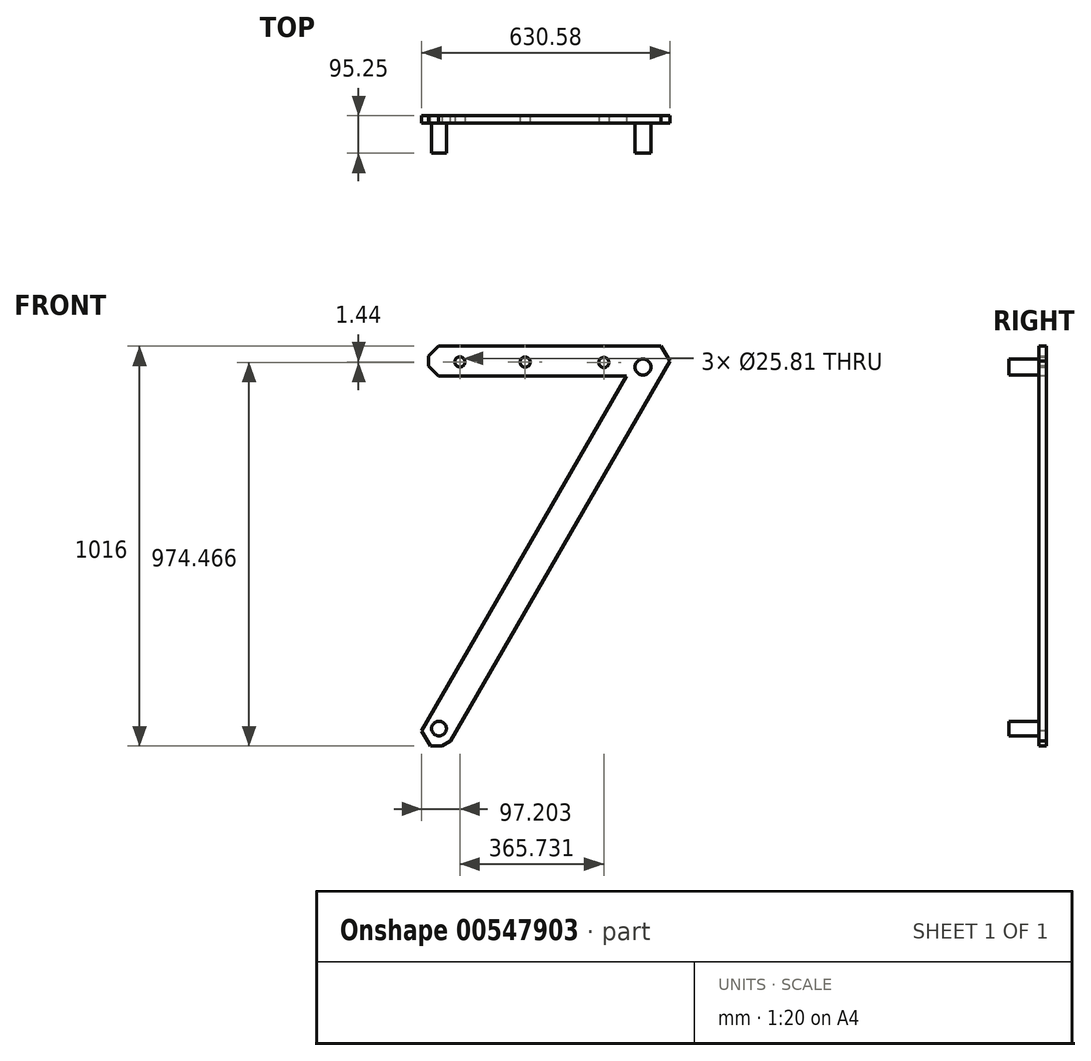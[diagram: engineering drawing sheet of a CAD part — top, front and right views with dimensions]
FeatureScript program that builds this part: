
annotation { "Feature Type Name" : "Feature", "Feature Type Description" : "" }
export const myFeature = defineFeature(function(context is Context, id is Id, definition is map)
    precondition{}
    {
        {
            var Q0;
            Q0=qCreatedBy(makeId("Front.planeOp"),FACE);
            var sketch = newSketch(context, id + "F0", { "sketchPlane" : qUnion([Q0])});
            skLineSegment(sketch, "E0", {"start": v(227.3, 546.1) * mm, "end": v(315.3, 546.1) * mm});
            skLineSegment(sketch, "E1", {"start": v(315.3, 546.1) * mm, "end": v(-271.3, -469.9) * mm});
            skLineSegment(sketch, "E2", {"start": v(-271.3, -469.9) * mm, "end": v(-359.29, -469.9) * mm});
            skLineSegment(sketch, "E3", {"start": v(-359.29, -469.9) * mm, "end": v(227.3, 546.1) * mm});
            skLineSegment(sketch, "E4", {"start": v(-66, 38.1) * mm, "end": v(0, 0) * mm, "construction": true});
            skSolve(sketch);
        }
        {
            var Q0;
            Q0 = qSketchRegion(id + "F0", true);
            extrude(context, id + "F1", {"entities" : qUnion([Q0]), "depth" : 19.05 * mm, "offsetDistance" : 25.4 * mm});
        }
        {
            var Q0;
            Q0=makeQuery(id+"F1.opExtrude","CAP_FACE",FACE,{"disambiguationData":[OSD([sQuery(id+"F0.wireOp",EDGE,"E0"),sQuery(id+"F0.wireOp",EDGE,"E1"),sQuery(id+"F0.wireOp",EDGE,"E2"),sQuery(id+"F0.wireOp",EDGE,"E3")])],"isStart":false});
            var sketch = newSketch(context, id + "F2", { "sketchPlane" : qUnion([Q0])});
            skLineSegment(sketch, "E5", {"start": v(-319.7, 546.1) * mm, "end": v(227.3, 546.1) * mm});
            skLineSegment(sketch, "E6", {"start": v(227.3, 546.1) * mm, "end": v(183.3, 469.9) * mm});
            skLineSegment(sketch, "E7", {"start": v(183.3, 469.9) * mm, "end": v(-319.7, 469.9) * mm});
            skLineSegment(sketch, "E8", {"start": v(-319.7, 469.9) * mm, "end": v(-319.7, 546.1) * mm});
            skSolve(sketch);
        }
        {
            var Q0;
            Q0 = qSketchRegion(id + "F2", true);
            var Q1;
            Q1=makeQuery(id+"F1.opExtrude","CAP_FACE",FACE,{"disambiguationData":[OSD([sQuery(id+"F0.wireOp",EDGE,"E0"),sQuery(id+"F0.wireOp",EDGE,"E1"),sQuery(id+"F0.wireOp",EDGE,"E2"),sQuery(id+"F0.wireOp",EDGE,"E3")])],"isStart":true});
            extrude(context, id + "F3", {"entities" : qUnion([Q0]), "operationType" : NewBodyOperationType.ADD, "endBound" : BoundingType.UP_TO_SURFACE, "oppositeDirection" : true, "depth" : 19.05 * mm, "endBoundEntityFace" : qUnion([Q1]), "offsetDistance" : 25.4 * mm});
        }
        {
            var Q0;
            Q0=makeQuery(id+"F3.boolean.opBoolean","MERGE",FACE,{"derivedFrom":[makeQuery(id+"F1.opExtrude","CAP_FACE",FACE,{"disambiguationData":[OSD([sQuery(id+"F0.wireOp",EDGE,"E0"),sQuery(id+"F0.wireOp",EDGE,"E1"),sQuery(id+"F0.wireOp",EDGE,"E2"),sQuery(id+"F0.wireOp",EDGE,"E3")])],"isStart":false}),makeQuery(id+"F3.opExtrude","CAP_FACE",FACE,{"disambiguationData":[OSD([sQuery(id+"F2.wireOp",EDGE,"E5"),sQuery(id+"F2.wireOp",EDGE,"E6"),sQuery(id+"F2.wireOp",EDGE,"E7"),sQuery(id+"F2.wireOp",EDGE,"E8")])],"isStart":true})]});
            var sketch = newSketch(context, id + "F4", { "sketchPlane" : qUnion([Q0])});
            skPoint(sketch, "E9", {"position": v(-240.09, 506) * mm});
            skPoint(sketch, "E10", {"position": v(-74.46, 505.55) * mm});
            skPoint(sketch, "E11", {"position": v(125.64, 504.57) * mm});
            skSolve(sketch);
        }
        {
            var Q0;
            Q0=sQuery(id+"F4.wireOp",VERTEX,"E9");
            var Q1;
            Q1=sQuery(id+"F4.wireOp",VERTEX,"E10");
            var Q2;
            Q2=sQuery(id+"F4.wireOp",VERTEX,"E11");
            var Q3;
            Q3=makeQuery(id+"F1.opExtrude","SWEPT_BODY",BODY,{"disambiguationData":[OSD([sQuery(id+"F0.wireOp",EDGE,"E0"),sQuery(id+"F0.wireOp",EDGE,"E1"),sQuery(id+"F0.wireOp",EDGE,"E2"),sQuery(id+"F0.wireOp",EDGE,"E3")])]});
            hole(context, id + "F5", {"style" : HoleStyle.SIMPLE, "endStyle" : HoleEndStyle.THROUGH, "standardTappedOrClearance" : lookupTablePath({ "standard" : "ANSI", "fit" : "Close", "size" : "1", "type" : "Clearance" }), "standardBlindInLast" : lookupTablePath({ "fit" : "Close", "standard" : "ANSI", "size" : "1", "type" : "Clearance" }), "holeDiameter" : 25.8 * mm, "isTappedThrough" : true, "tappedDepth" : 12.7 * mm, "tapClearance" : 3, "locations" : qUnion([Q0, Q1, Q2]), "scope" : qUnion([Q3])});
        }
        {
            var Q0;
            Q0=makeQuery(id+"F3.boolean.opBoolean","MERGE",FACE,{"derivedFrom":[makeQuery(id+"F1.opExtrude","CAP_FACE",FACE,{"disambiguationData":[OSD([sQuery(id+"F0.wireOp",EDGE,"E0"),sQuery(id+"F0.wireOp",EDGE,"E1"),sQuery(id+"F0.wireOp",EDGE,"E2"),sQuery(id+"F0.wireOp",EDGE,"E3")])],"isStart":false}),makeQuery(id+"F3.opExtrude","CAP_FACE",FACE,{"disambiguationData":[OSD([sQuery(id+"F2.wireOp",EDGE,"E5"),sQuery(id+"F2.wireOp",EDGE,"E6"),sQuery(id+"F2.wireOp",EDGE,"E7"),sQuery(id+"F2.wireOp",EDGE,"E8")])],"isStart":true})]});
            cPlane(context, id + "F6", {"entities" : qUnion([Q0]), "cplaneType" : CPlaneType.OFFSET, "offset" : 76.2 * mm, "width" : 152.4 * mm, "height" : 152.4 * mm});
        }
        {
            var Q0;
            Q0=qCreatedBy(id+"F6.planeOp",FACE);
            var sketch = newSketch(context, id + "F7", { "sketchPlane" : qUnion([Q0])});
            skCircle(sketch, "E12", {"center": v(225, 492.94) * mm, "radius": 20.51 * mm});
            skCircle(sketch, "E13", {"center": v(-293.25, -425.56) * mm, "radius": 18.71 * mm});
            skSolve(sketch);
        }
        {
            var Q0;
            Q0 = qSketchRegion(id + "F7", true);
            var Q1;
            Q1=makeQuery(id+"F3.boolean.opBoolean","MERGE",FACE,{"derivedFrom":[makeQuery(id+"F1.opExtrude","CAP_FACE",FACE,{"disambiguationData":[OSD([sQuery(id+"F0.wireOp",EDGE,"E0"),sQuery(id+"F0.wireOp",EDGE,"E1"),sQuery(id+"F0.wireOp",EDGE,"E2"),sQuery(id+"F0.wireOp",EDGE,"E3")])],"isStart":false}),makeQuery(id+"F3.opExtrude","CAP_FACE",FACE,{"disambiguationData":[OSD([sQuery(id+"F2.wireOp",EDGE,"E5"),sQuery(id+"F2.wireOp",EDGE,"E6"),sQuery(id+"F2.wireOp",EDGE,"E7"),sQuery(id+"F2.wireOp",EDGE,"E8")])],"isStart":true})]});
            extrude(context, id + "F8", {"entities" : qUnion([Q0]), "operationType" : NewBodyOperationType.ADD, "endBound" : BoundingType.UP_TO_SURFACE, "oppositeDirection" : true, "depth" : 25.4 * mm, "endBoundEntityFace" : qUnion([Q1]), "offsetDistance" : 25.4 * mm});
        }
        {
            var Q0;
            Q0=makeQuery(id+"F3.opExtrude","SWEPT_EDGE",EDGE,{"disambiguationData":[OSD([sQuery(id+"F2.wireOp",EDGE,"E5"),sQuery(id+"F2.wireOp",EDGE,"E8")])]});
            var Q1;
            Q1=makeQuery(id+"F1.opExtrude","SWEPT_EDGE",EDGE,{"disambiguationData":[OSD([sQuery(id+"F0.wireOp",EDGE,"E1"),sQuery(id+"F0.wireOp",EDGE,"E2")])]});
            var Q2;
            Q2=makeQuery(id+"F1.opExtrude","SWEPT_EDGE",EDGE,{"disambiguationData":[OSD([sQuery(id+"F0.wireOp",EDGE,"E0"),sQuery(id+"F0.wireOp",EDGE,"E1")])]});
            var Q3;
            Q3=makeQuery(id+"F1.opExtrude","SWEPT_EDGE",EDGE,{"disambiguationData":[OSD([sQuery(id+"F0.wireOp",EDGE,"E2"),sQuery(id+"F0.wireOp",EDGE,"E3")])]});
            var Q4;
            Q4=makeQuery(id+"F3.opExtrude","SWEPT_EDGE",EDGE,{"disambiguationData":[OSD([sQuery(id+"F2.wireOp",EDGE,"E7"),sQuery(id+"F2.wireOp",EDGE,"E8")])]});
            chamfer(context, id + "F9", {"entities" : qUnion([Q0, Q1, Q2, Q3, Q4]), "width" : 25.4 * mm, "tangentPropagation" : true});
        }
    });
